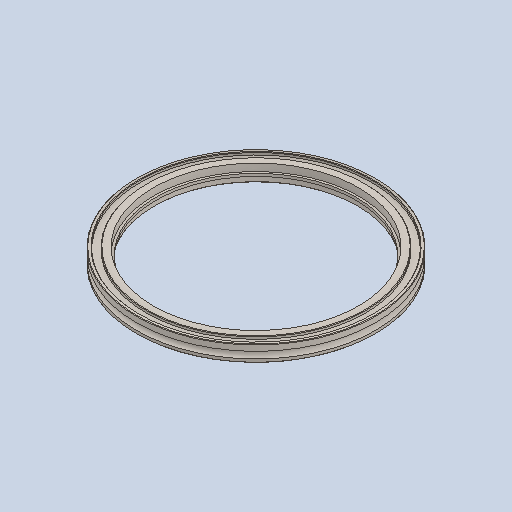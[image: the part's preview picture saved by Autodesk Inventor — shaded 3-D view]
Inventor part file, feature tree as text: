
AUTODESK INVENTOR PART (.ipt)
format: ipt  version: 2023 (Build 270158000, 158)  size: 164,352 bytes
history: native  units: in
note: dims shown in document units (in); Inventor stores cm internally (conversion verified against a paired STEP export)
features: extrude x1
ambient origin geometry x8: Origin, YZ Plane, XZ Plane, XY Plane, X Axis, Y Axis, Z Axis, Center Point
bodies: Solid1 (feature_tree)
feature tree (1):
  extrude  "Extrude2"  [1 undecoded]
note: 1 required parameter value undecoded (feature->parameter linkage not recoverable at this tier; creation-order binding heuristic only, values carry confidence <= 0.55)
